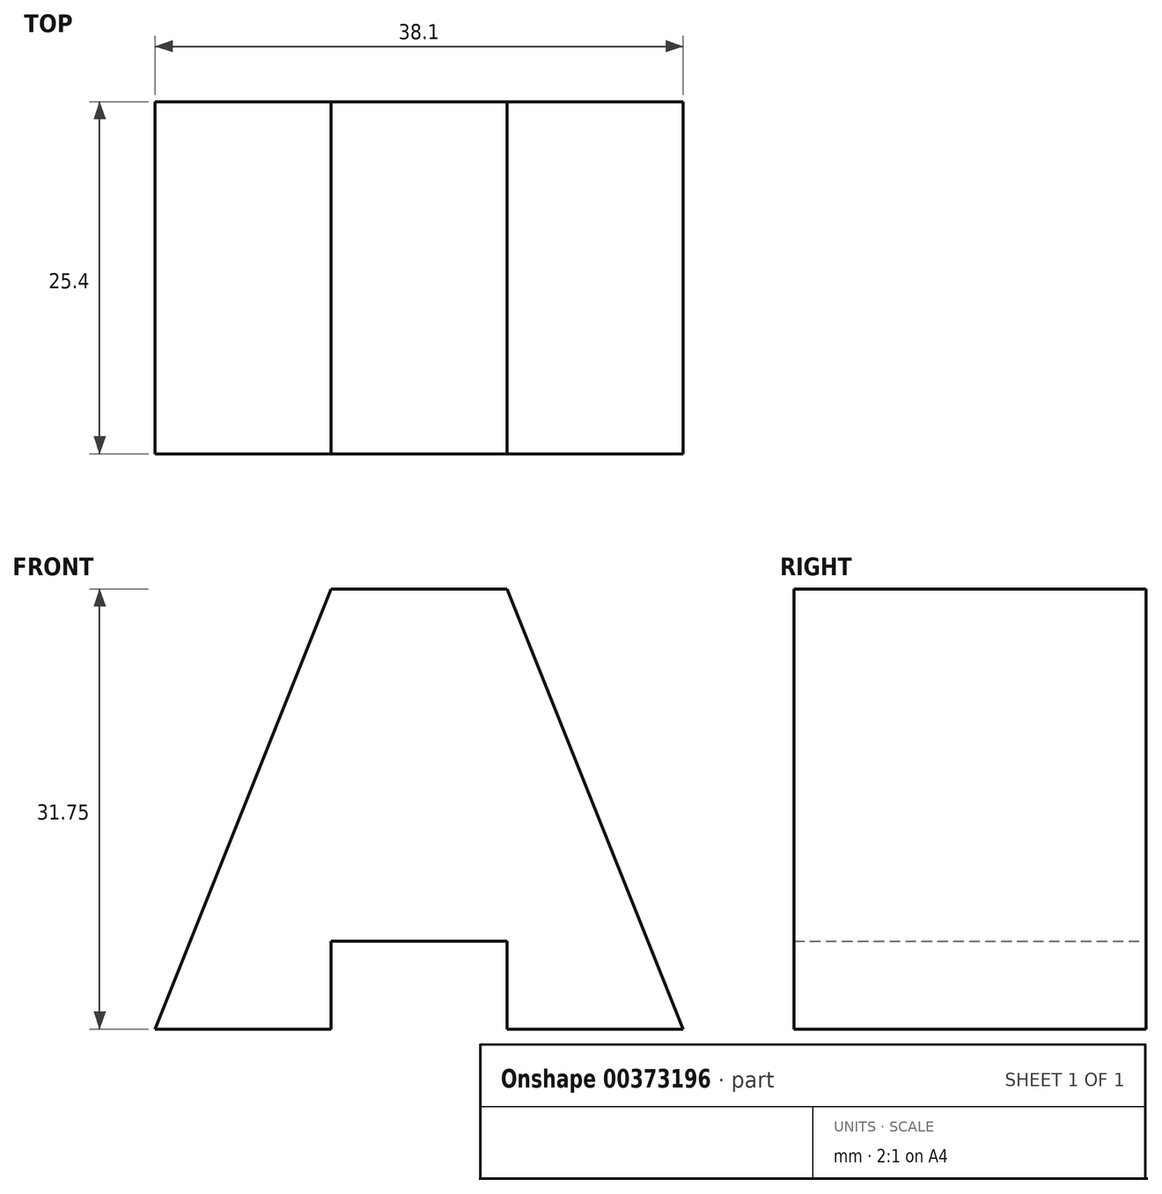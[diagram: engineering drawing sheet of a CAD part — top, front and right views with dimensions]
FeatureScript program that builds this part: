
annotation { "Feature Type Name" : "Feature", "Feature Type Description" : "" }
export const myFeature = defineFeature(function(context is Context, id is Id, definition is map)
    precondition{}
    {
        {
            var Q0;
            Q0=qCreatedBy(makeId("Front.planeOp"),FACE);
            var sketch = newSketch(context, id + "F0", { "sketchPlane" : qUnion([Q0])});
            skLineSegment(sketch, "E0", {"start": v(0, 0) * mm, "end": v(12.7, 0) * mm});
            skLineSegment(sketch, "E1", {"start": v(12.7, 0) * mm, "end": v(12.7, 6.35) * mm});
            skLineSegment(sketch, "E2", {"start": v(12.7, 6.35) * mm, "end": v(25.4, 6.35) * mm});
            skLineSegment(sketch, "E3", {"start": v(25.4, 6.35) * mm, "end": v(25.4, 0) * mm});
            skLineSegment(sketch, "E4", {"start": v(25.4, 0) * mm, "end": v(38.1, 0) * mm});
            skLineSegment(sketch, "E5", {"start": v(38.1, 0) * mm, "end": v(25.4, 31.75) * mm});
            skLineSegment(sketch, "E6", {"start": v(25.4, 31.75) * mm, "end": v(12.7, 31.75) * mm});
            skLineSegment(sketch, "E7", {"start": v(12.7, 31.75) * mm, "end": v(0, 0) * mm});
            skSolve(sketch);
        }
        {
            var Q0;
            Q0 = qSketchRegion(id + "F0", true);
            extrude(context, id + "F1", {"entities" : qUnion([Q0]), "depth" : 25.4 * mm});
        }
    });
